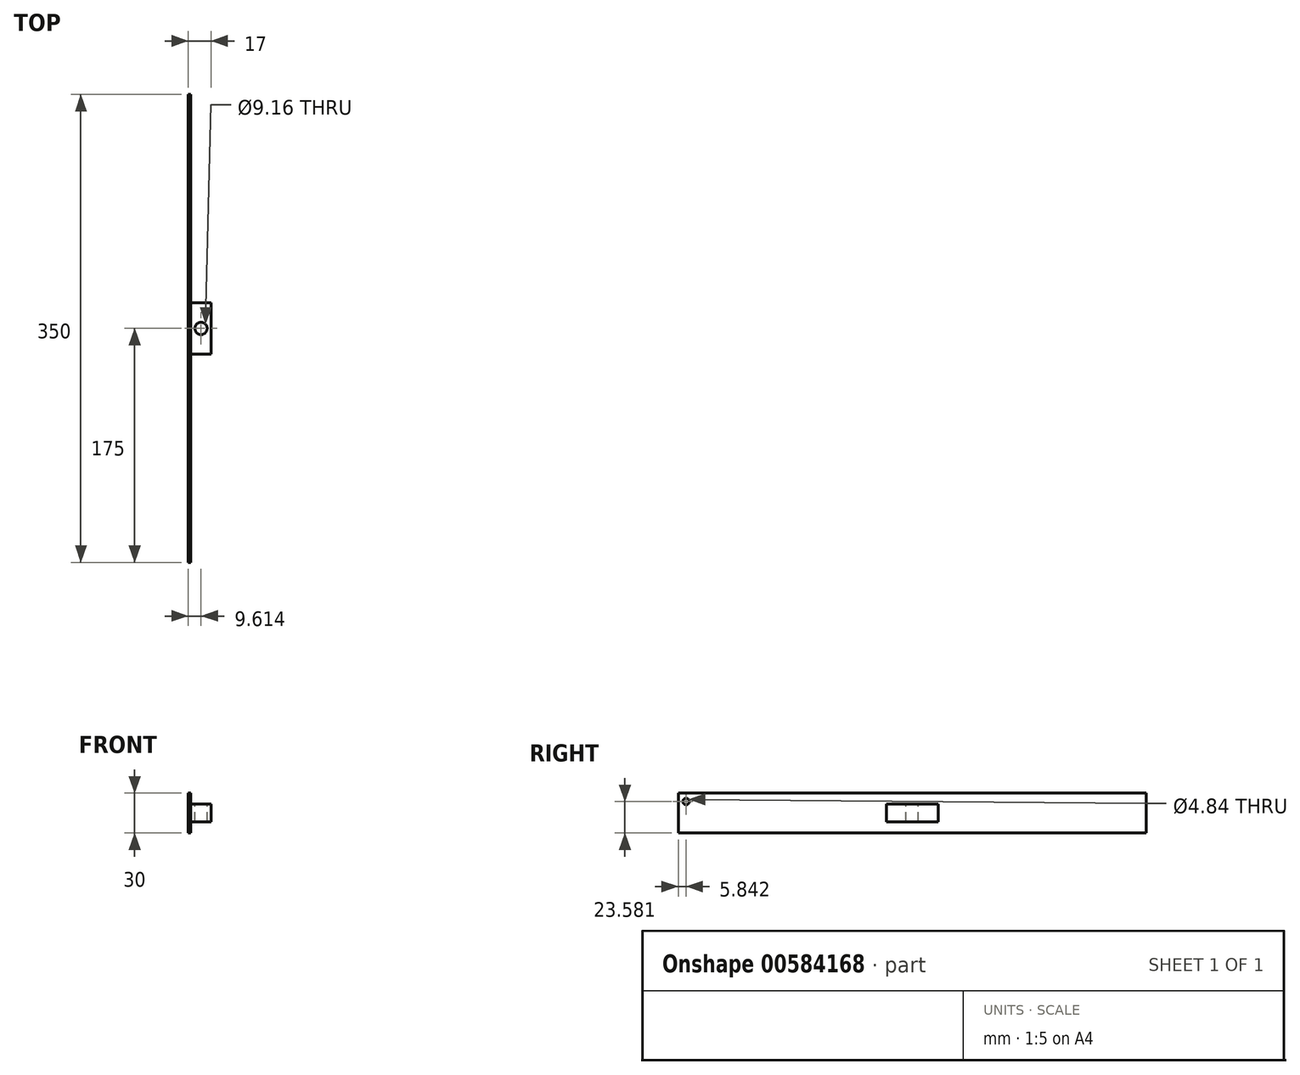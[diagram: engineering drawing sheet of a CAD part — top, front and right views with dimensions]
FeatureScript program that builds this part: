
annotation { "Feature Type Name" : "Feature", "Feature Type Description" : "" }
export const myFeature = defineFeature(function(context is Context, id is Id, definition is map)
    precondition{}
    {
        {
            var Q0;
            Q0=qCreatedBy(makeId("Right.planeOp"),FACE);
            var sketch = newSketch(context, id + "F0", { "sketchPlane" : qUnion([Q0])});
            skLineSegment(sketch, "E0.bottom", {"start": v(175, -15) * mm, "end": v(-175, -15) * mm});
            skLineSegment(sketch, "E0.top", {"start": v(175, 15) * mm, "end": v(-175, 15) * mm});
            skLineSegment(sketch, "E0.left", {"start": v(175, -15) * mm, "end": v(175, 15) * mm});
            skLineSegment(sketch, "E0.right", {"start": v(-175, -15) * mm, "end": v(-175, 15) * mm});
            skPoint(sketch, "E0.middle", {"position": v(0, 0) * mm});
            skCircle(sketch, "E1", {"center": v(-169.16, 8.58) * mm, "radius": 2.42 * mm});
            skSolve(sketch);
        }
        {
            var Q0;
            Q0 = qSketchRegion(id + "F0", true);
            extrude(context, id + "F1", {"entities" : qUnion([Q0]), "depth" : 2 * mm, "offsetDistance" : 25 * mm});
        }
        {
            var Q0;
            Q0=makeQuery(id+"F1.opExtrude","CAP_FACE",FACE,{"disambiguationData":[OSD([sQuery(id+"F0.wireOp",EDGE,"E0.bottom"),sQuery(id+"F0.wireOp",EDGE,"E0.top"),sQuery(id+"F0.wireOp",EDGE,"E0.left"),sQuery(id+"F0.wireOp",EDGE,"E0.right"),sQuery(id+"F0.wireOp",EDGE,"E1")])],"isStart":false});
            var sketch = newSketch(context, id + "F2", { "sketchPlane" : qUnion([Q0])});
            skLineSegment(sketch, "E2.bottom", {"start": v(19.3, -6.7) * mm, "end": v(-19.3, -6.7) * mm});
            skLineSegment(sketch, "E2.top", {"start": v(19.3, 6.7) * mm, "end": v(-19.3, 6.7) * mm});
            skLineSegment(sketch, "E2.left", {"start": v(19.3, -6.7) * mm, "end": v(19.3, 6.7) * mm});
            skLineSegment(sketch, "E2.right", {"start": v(-19.3, -6.7) * mm, "end": v(-19.3, 6.7) * mm});
            skPoint(sketch, "E2.middle", {"position": v(0, 0) * mm});
            skSolve(sketch);
        }
        {
            var Q0;
            Q0=makeQuery(id+"F2.imprint","IMPRINT",FACE,{"disambiguationData":[TD([[makeQuery(id+"F2.imprint","IMPRINT",EDGE,{"derivedFrom":sQuery(id+"F2.wireOp",EDGE,"E2.bottom")}),-1.0]])]});
            extrude(context, id + "F3", {"entities" : qUnion([Q0]), "operationType" : NewBodyOperationType.ADD, "depth" : 15 * mm, "offsetDistance" : 25 * mm});
        }
        {
            var Q0;
            Q0=makeQuery(id+"F3.opExtrude","SWEPT_FACE",FACE,{"disambiguationData":[OSD([sQuery(id+"F2.wireOp",EDGE,"E2.top")])]});
            var sketch = newSketch(context, id + "F4", { "sketchPlane" : qUnion([Q0])});
            skCircle(sketch, "E3", {"center": v(9.61, 0) * mm, "radius": 4.58 * mm});
            skSolve(sketch);
        }
        {
            var Q0;
            Q0=makeQuery(id+"F4.imprint","IMPRINT",FACE,{"disambiguationData":[TD([[makeQuery(id+"F4.imprint","IMPRINT",EDGE,{"derivedFrom":sQuery(id+"F4.wireOp",EDGE,"E3")}),1.0]])]});
            extrude(context, id + "F5", {"entities" : qUnion([Q0]), "operationType" : NewBodyOperationType.REMOVE, "endBound" : BoundingType.THROUGH_ALL, "oppositeDirection" : true, "depth" : 25 * mm, "offsetDistance" : 25 * mm});
        }
    });
